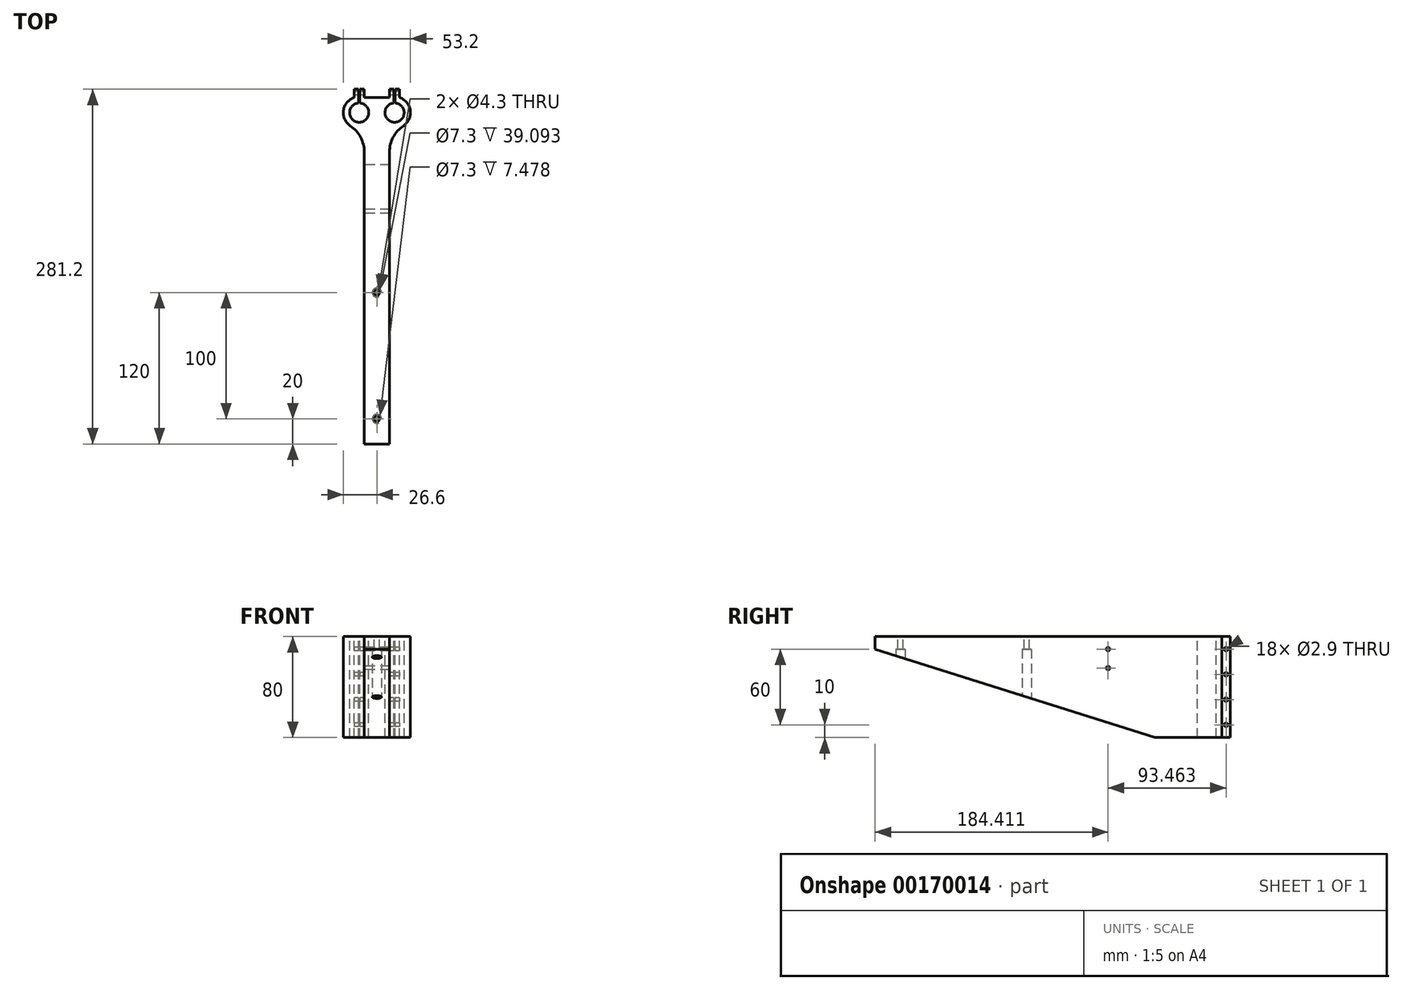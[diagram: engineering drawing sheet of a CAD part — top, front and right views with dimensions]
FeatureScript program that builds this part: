
annotation { "Feature Type Name" : "Feature", "Feature Type Description" : "" }
export const myFeature = defineFeature(function(context is Context, id is Id, definition is map)
    precondition{}
    {
        {
            var Q0;
            Q0=qCreatedBy(makeId("Top.planeOp"),FACE);
            var sketch = newSketch(context, id + "F0", { "sketchPlane" : qUnion([Q0])});
            skCircle(sketch, "E0", {"center": v(0, 0) * mm, "radius": 7.6 * mm});
            skArc(sketch, "E1.0", {"start": v(-4, 11.95) * mm, "mid": v(-12.49, 1.7) * mm, "end": v(-7.04, -10.45) * mm});
            skLineSegment(sketch, "E2.top", {"start": v(4, 18.6) * mm, "end": v(-4, 18.6) * mm});
            skLineSegment(sketch, "E2.left", {"start": v(4, 11.95) * mm, "end": v(4, 18.6) * mm});
            skLineSegment(sketch, "E2.right", {"start": v(-4, 11.95) * mm, "end": v(-4, 18.6) * mm});
            skPoint(sketch, "E2.middle", {"position": v(0, 12.6) * mm});
            skLineSegment(sketch, "E3.top", {"start": v(4, -262.6) * mm, "end": v(24, -262.6) * mm});
            skCircle(sketch, "E4", {"center": v(28, 0) * mm, "radius": 7.6 * mm});
            skArc(sketch, "E5.0", {"start": v(35.04, -10.45) * mm, "mid": v(40.49, 1.7) * mm, "end": v(32, 11.95) * mm});
            skLineSegment(sketch, "E6.bottom", {"start": v(24, 18.6) * mm, "end": v(32, 18.6) * mm});
            skLineSegment(sketch, "E6.left", {"start": v(24, 18.6) * mm, "end": v(24, 11.95) * mm});
            skLineSegment(sketch, "E6.right", {"start": v(32, 18.6) * mm, "end": v(32, 11.95) * mm});
            skLineSegment(sketch, "E7", {"start": v(4, 11.95) * mm, "end": v(24, 11.95) * mm});
            skLineSegment(sketch, "E8", {"start": v(4, -31.19) * mm, "end": v(4, -262.6) * mm});
            skLineSegment(sketch, "E9", {"start": v(24, -262.6) * mm, "end": v(24, -31.19) * mm});
            skPoint(sketch, "E10.visualSharp", {"position": v(4, -11.95) * mm});
            skArc(sketch, "E10.filletArc", {"start": v(4, -31.19) * mm, "mid": v(1.07, -19.44) * mm, "end": v(-7.04, -10.45) * mm});
            skPoint(sketch, "E11.visualSharp", {"position": v(24, -11.95) * mm});
            skArc(sketch, "E11.filletArc", {"start": v(35.04, -10.45) * mm, "mid": v(26.93, -19.44) * mm, "end": v(24, -31.19) * mm});
            skSolve(sketch);
        }
        {
            var Q0;
            Q0=makeQuery(id+"F0.imprint","IMPRINT",FACE,{"disambiguationData":[TD([[makeQuery(id+"F0.imprint","IMPRINT",EDGE,{"derivedFrom":sQuery(id+"F0.wireOp",EDGE,"E3.top")}),1.0]])]});
            extrude(context, id + "F1", {"entities" : qUnion([Q0]), "oppositeDirection" : true, "depth" : 80 * mm});
        }
        {
            var Q0;
            Q0=makeQuery(id+"F0.imprint","IMPRINT",FACE,{"disambiguationData":[TD([[makeQuery(id+"F0.imprint","IMPRINT",EDGE,{"derivedFrom":sQuery(id+"F0.wireOp",EDGE,"E0")}),-1.0]])]});
            extrude(context, id + "F2", {"entities" : qUnion([Q0]), "operationType" : NewBodyOperationType.ADD, "oppositeDirection" : true, "depth" : 80 * mm});
        }
        {
            var Q0;
            {var subQ0=sQuery(id+"F0.wireOp",EDGE,"E1.0");Q0=makeQuery(id+"F2.boolean.opBoolean","MERGE",FACE,{"derivedFrom":[makeQuery(id+"F1.opExtrude","CAP_FACE",FACE,{"disambiguationData":[OSD([subQ0,sQuery(id+"F0.wireOp",EDGE,"E3.top"),sQuery(id+"F0.wireOp",EDGE,"E3.left"),sQuery(id+"F0.wireOp",EDGE,"E3.right")])],"isStart":true}),makeQuery(id+"F2.opExtrude","CAP_FACE",FACE,{"disambiguationData":[OSD([sQuery(id+"F0.wireOp",EDGE,"E0"),subQ0,sQuery(id+"F0.wireOp",EDGE,"E2.top"),sQuery(id+"F0.wireOp",EDGE,"E2.left"),sQuery(id+"F0.wireOp",EDGE,"E2.right")])],"isStart":true})]});}
            var sketch = newSketch(context, id + "F3", { "sketchPlane" : qUnion([Q0])});
            skCircle(sketch, "E12", {"center": v(14, -142.6) * mm, "radius": 2.15 * mm});
            skCircle(sketch, "E13", {"center": v(14, -242.6) * mm, "radius": 2.15 * mm});
            skSolve(sketch);
        }
        {
            var Q0;
            Q0=qSketchRegion(id+"F3",true);
            extrude(context, id + "F4", {"entities" : qUnion([Q0]), "operationType" : NewBodyOperationType.REMOVE, "endBound" : BoundingType.THROUGH_ALL, "oppositeDirection" : true, "depth" : 25 * mm});
        }
        {
            var Q0;
            Q0=makeQuery(id+"F1.opExtrude","CAP_FACE",FACE,{"disambiguationData":[OSD([sQuery(id+"F0.wireOp",EDGE,"E0"),sQuery(id+"F0.wireOp",EDGE,"E1.0"),sQuery(id+"F0.wireOp",EDGE,"E2.top"),sQuery(id+"F0.wireOp",EDGE,"E2.left"),sQuery(id+"F0.wireOp",EDGE,"E2.right"),sQuery(id+"F0.wireOp",EDGE,"E3.top"),sQuery(id+"F0.wireOp",EDGE,"E3.left"),sQuery(id+"F0.wireOp",EDGE,"E3.right")])],"isStart":false});
            var sketch = newSketch(context, id + "F5", { "sketchPlane" : qUnion([Q0])});
            skCircle(sketch, "E14", {"center": v(14, 242.6) * mm, "radius": 3.65 * mm});
            skCircle(sketch, "E15", {"center": v(14, 142.6) * mm, "radius": 3.65 * mm});
            skSolve(sketch);
        }
        {
            var Q0;
            Q0=makeQuery(id+"F5.imprint","IMPRINT",FACE,{"disambiguationData":[TD([[makeQuery(id+"F5.imprint","IMPRINT",EDGE,{"derivedFrom":sQuery(id+"F5.wireOp",EDGE,"E14")}),1.0]])]});
            var Q1;
            Q1=makeQuery(id+"F5.imprint","IMPRINT",FACE,{"disambiguationData":[TD([[makeQuery(id+"F5.imprint","IMPRINT",EDGE,{"derivedFrom":sQuery(id+"F5.wireOp",EDGE,"E15")}),1.0]])]});
            extrude(context, id + "F6", {"entities" : qUnion([Q0, Q1]), "operationType" : NewBodyOperationType.REMOVE, "oppositeDirection" : true, "depth" : (80 - 10) * mm});
        }
        {
            var Q0;
            Q0=makeQuery(id+"F1.opExtrude","SWEPT_FACE",FACE,{"disambiguationData":[OSD([sQuery(id+"F0.wireOp",EDGE,"E8")])]});
            var sketch = newSketch(context, id + "F7", { "sketchPlane" : qUnion([Q0])});
            skLineSegment(sketch, "E16", {"start": v(262.6, 0) * mm, "end": v(262.6, -10) * mm});
            skLineSegment(sketch, "E17", {"start": v(31.19, -80) * mm, "end": v(41.19, -80) * mm});
            skLineSegment(sketch, "E18", {"start": v(262.6, -10) * mm, "end": v(41.19, -80) * mm});
            skSolve(sketch);
        }
        {
            var Q0;
            {var subQ0=sQuery(id+"F7.wireOp",EDGE,"E18");Q0=makeQuery(id+"F7.imprint","IMPRINT",FACE,{"disambiguationData":[TD([[makeQuery(id+"F7.imprint","IMPRINT",EDGE,{"derivedFrom":subQ0}),1.0]])]});}
            extrude(context, id + "F8", {"entities" : qUnion([Q0]), "operationType" : NewBodyOperationType.REMOVE, "endBound" : BoundingType.THROUGH_ALL, "oppositeDirection" : true, "depth" : 25 * mm});
        }
        {
            var Q0;
            Q0=makeQuery(id+"F1.opExtrude","CAP_FACE",FACE,{"disambiguationData":[OSD([sQuery(id+"F0.wireOp",EDGE,"E0"),sQuery(id+"F0.wireOp",EDGE,"E1.0"),sQuery(id+"F0.wireOp",EDGE,"E2.top"),sQuery(id+"F0.wireOp",EDGE,"E2.left"),sQuery(id+"F0.wireOp",EDGE,"E2.right"),sQuery(id+"F0.wireOp",EDGE,"E3.top"),sQuery(id+"F0.wireOp",EDGE,"E3.left"),sQuery(id+"F0.wireOp",EDGE,"E3.right")])],"isStart":true});
            var sketch = newSketch(context, id + "F9", { "sketchPlane" : qUnion([Q0])});
            skLineSegment(sketch, "E19.bottom", {"start": v(0, 18.6) * mm, "end": v(-0.5, 18.6) * mm});
            skLineSegment(sketch, "E19.top", {"start": v(0, 0) * mm, "end": v(-0.5, 0) * mm});
            skLineSegment(sketch, "E19.left", {"start": v(0, 18.6) * mm, "end": v(0, 0) * mm});
            skLineSegment(sketch, "E19.right", {"start": v(-0.5, 18.6) * mm, "end": v(-0.5, 0) * mm});
            skLineSegment(sketch, "E20.MirrorCS", {"start": v(0.5, 18.6) * mm, "end": v(0.5, 0) * mm});
            skLineSegment(sketch, "E21.MirrorCS", {"start": v(0, 0) * mm, "end": v(0.5, 0) * mm});
            skLineSegment(sketch, "E22.MirrorCS", {"start": v(0, 18.6) * mm, "end": v(0.5, 18.6) * mm});
            skLineSegment(sketch, "E23", {"start": v(14, 11.95) * mm, "end": v(14, -10.83) * mm, "construction": true});
            skLineSegment(sketch, "E24.MirrorCS", {"start": v(28, 18.6) * mm, "end": v(27.5, 18.6) * mm});
            skLineSegment(sketch, "E25.MirrorCS", {"start": v(28, 18.6) * mm, "end": v(28.5, 18.6) * mm});
            skLineSegment(sketch, "E26.MirrorCS", {"start": v(28, 0) * mm, "end": v(27.5, 0) * mm});
            skLineSegment(sketch, "E27.MirrorCS", {"start": v(28, 0) * mm, "end": v(28.5, 0) * mm});
            skLineSegment(sketch, "E28.MirrorCS", {"start": v(28, 18.6) * mm, "end": v(28, 0) * mm});
            skLineSegment(sketch, "E29.MirrorCS", {"start": v(28.5, 18.6) * mm, "end": v(28.5, 0) * mm});
            skLineSegment(sketch, "E30.MirrorCS", {"start": v(27.5, 18.6) * mm, "end": v(27.5, 0) * mm});
            skSolve(sketch);
        }
        {
            var Q0;
            Q0 = qSketchRegion(id + "F9", true);
            extrude(context, id + "F10", {"entities" : qUnion([Q0]), "operationType" : NewBodyOperationType.REMOVE, "endBound" : BoundingType.THROUGH_ALL, "oppositeDirection" : true, "depth" : 25 * mm});
        }
        {
            var Q0;
            Q0=makeQuery(id+"F1.opExtrude","SWEPT_FACE",FACE,{"disambiguationData":[OSD([sQuery(id+"F0.wireOp",EDGE,"E2.right")])]});
            var sketch = newSketch(context, id + "F11", { "sketchPlane" : qUnion([Q0])});
            skCircle(sketch, "E31", {"center": v(-15.27, -30) * mm, "radius": 1.45 * mm});
            skCircle(sketch, "E32", {"center": v(-15.27, -70) * mm, "radius": 1.45 * mm});
            skCircle(sketch, "E33.0", {"center": v(-15.27, -30) * mm, "radius": 2.45 * mm});
            skCircle(sketch, "E34.0", {"center": v(-15.27, -70) * mm, "radius": 2.45 * mm});
            skCircle(sketch, "E35", {"center": v(-15.27, -10) * mm, "radius": 1.45 * mm});
            skCircle(sketch, "E36", {"center": v(-15.27, -10) * mm, "radius": 2.45 * mm});
            skCircle(sketch, "E37", {"center": v(-15.27, -50) * mm, "radius": 1.45 * mm});
            skCircle(sketch, "E38", {"center": v(-15.27, -50) * mm, "radius": 2.45 * mm});
            skSolve(sketch);
        }
        {
            var Q0;
            Q0=makeQuery(id+"F11.imprint","IMPRINT",FACE,{"disambiguationData":[TD([[makeQuery(id+"F11.imprint","IMPRINT",EDGE,{"derivedFrom":sQuery(id+"F11.wireOp",EDGE,"E31")}),1.0]])]});
            var Q1;
            Q1=makeQuery(id+"F11.imprint","IMPRINT",FACE,{"disambiguationData":[TD([[makeQuery(id+"F11.imprint","IMPRINT",EDGE,{"derivedFrom":sQuery(id+"F11.wireOp",EDGE,"E32")}),1.0]])]});
            var Q2;
            Q2=makeQuery(id+"F11.imprint","IMPRINT",FACE,{"disambiguationData":[TD([[makeQuery(id+"F11.imprint","IMPRINT",EDGE,{"derivedFrom":sQuery(id+"F11.wireOp",EDGE,"E37")}),1.0]])]});
            var Q3;
            Q3=makeQuery(id+"F11.imprint","IMPRINT",FACE,{"disambiguationData":[TD([[makeQuery(id+"F11.imprint","IMPRINT",EDGE,{"derivedFrom":sQuery(id+"F11.wireOp",EDGE,"E35")}),1.0]])]});
            extrude(context, id + "F12", {"entities" : qUnion([Q0, Q1, Q2, Q3]), "operationType" : NewBodyOperationType.REMOVE, "endBound" : BoundingType.THROUGH_ALL, "oppositeDirection" : true, "depth" : 25 * mm});
        }
        {
            var Q0;
            Q0=makeQuery(id+"F1.opExtrude","SWEPT_FACE",FACE,{"disambiguationData":[OSD([sQuery(id+"F0.wireOp",EDGE,"E8")])]});
            var sketch = newSketch(context, id + "F13", { "sketchPlane" : qUnion([Q0])});
            skCircle(sketch, "E39", {"center": v(78.19, -10) * mm, "radius": 1.45 * mm});
            skCircle(sketch, "E40", {"center": v(78.19, -25) * mm, "radius": 1.45 * mm});
            skSolve(sketch);
        }
        {
            var Q0;
            Q0=makeQuery(id+"F13.imprint","IMPRINT",FACE,{"disambiguationData":[TD([[makeQuery(id+"F13.imprint","IMPRINT",EDGE,{"derivedFrom":sQuery(id+"F13.wireOp",EDGE,"E39")}),1.0]])]});
            var Q1;
            Q1=makeQuery(id+"F13.imprint","IMPRINT",FACE,{"disambiguationData":[TD([[makeQuery(id+"F13.imprint","IMPRINT",EDGE,{"derivedFrom":sQuery(id+"F13.wireOp",EDGE,"E40")}),1.0]])]});
            extrude(context, id + "F14", {"entities" : qUnion([Q0, Q1]), "operationType" : NewBodyOperationType.REMOVE, "endBound" : BoundingType.THROUGH_ALL, "oppositeDirection" : true, "depth" : 25 * mm});
        }
    });
